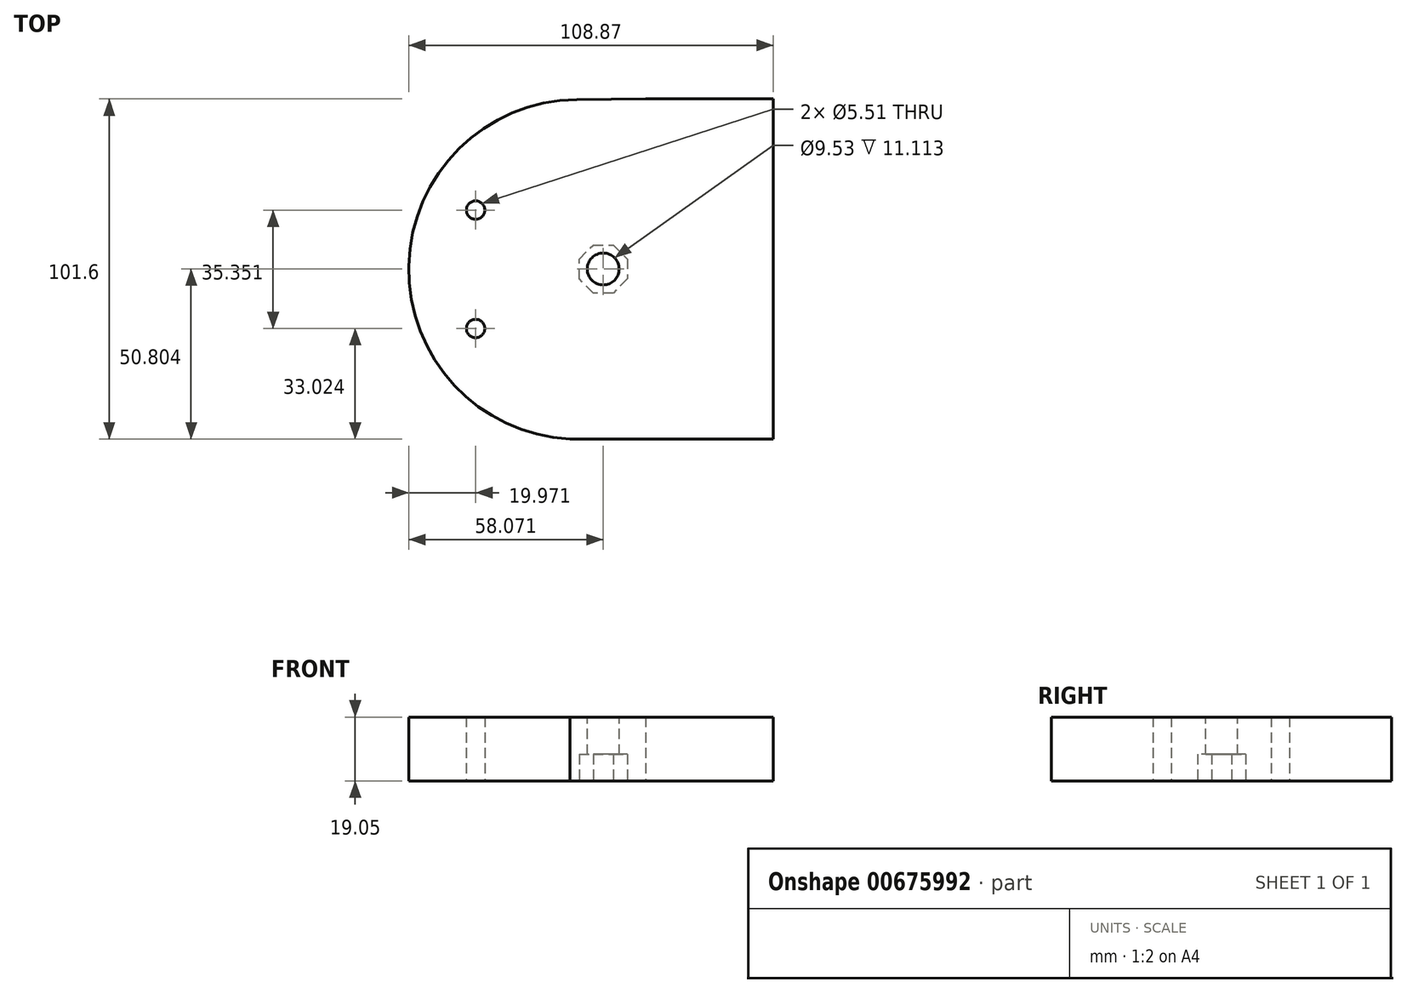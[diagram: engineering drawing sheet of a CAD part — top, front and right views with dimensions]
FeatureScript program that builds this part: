
annotation { "Feature Type Name" : "Feature", "Feature Type Description" : "" }
export const myFeature = defineFeature(function(context is Context, id is Id, definition is map)
    precondition{}
    {
        {
            var Q0;
            Q0=qCreatedBy(makeId("Top.planeOp"),FACE);
            var sketch = newSketch(context, id + "F0", { "sketchPlane" : qUnion([Q0])});
            skArc(sketch, "E0", {"start": v(-76.55, 44.5) * mm, "mid": v(-126.76, -5.22) * mm, "end": v(-78.58, -56.9) * mm});
            skLineSegment(sketch, "E1", {"start": v(-76.55, 44.5) * mm, "end": v(-56, 44.7) * mm});
            skLineSegment(sketch, "E2", {"start": v(-56, 44.7) * mm, "end": v(-56, -56.9) * mm});
            skLineSegment(sketch, "E3", {"start": v(-56, -56.9) * mm, "end": v(-78.58, -56.9) * mm});
            skCircle(sketch, "E4", {"center": v(-106.8, 11.47) * mm, "radius": 2.76 * mm});
            skCircle(sketch, "E5", {"center": v(-106.8, -23.88) * mm, "radius": 2.76 * mm});
            skSolve(sketch);
        }
        {
            var Q0;
            Q0 = qSketchRegion(id + "F0", true);
            extrude(context, id + "F1", {"entities" : qUnion([Q0]), "depth" : 19.05 * mm, "offsetDistance" : 25.4 * mm});
        }
        {
            var Q0;
            Q0=makeQuery(id+"F1.opExtrude","SWEPT_FACE",FACE,{"disambiguationData":[OSD([sQuery(id+"F0.wireOp",EDGE,"E2")])]});
            extrude(context, id + "F2", {"entities" : qUnion([Q0]), "operationType" : NewBodyOperationType.ADD, "depth" : 12.7 * mm, "offsetDistance" : 25.4 * mm});
        }
        {
            var Q0;
            Q0=makeQuery(id+"F2.opExtrude","CAP_FACE",FACE,{"disambiguationData":[OSD([sQuery(id+"F0.wireOp",EDGE,"E2")])],"isStart":false});
            extrude(context, id + "F3", {"entities" : qUnion([Q0]), "operationType" : NewBodyOperationType.ADD, "depth" : 25.4 * mm, "offsetDistance" : 25.4 * mm});
        }
        {
            var Q0;
            {var subQ0=sQuery(id+"F0.wireOp",EDGE,"E2");var subQ1=makeQuery(id+"F1.opExtrude","CAP_EDGE",EDGE,{"disambiguationData":[OSD([subQ0])],"isStart":false});Q0=makeQuery(id+"F3.boolean.opBoolean","MERGE",FACE,{"derivedFrom":[makeQuery(id+"F2.boolean.opBoolean","MERGE",FACE,{"derivedFrom":[makeQuery(id+"F1.opExtrude","CAP_FACE",FACE,{"disambiguationData":[OSD([sQuery(id+"F0.wireOp",EDGE,"E0"),sQuery(id+"F0.wireOp",EDGE,"E1"),subQ0,sQuery(id+"F0.wireOp",EDGE,"E3"),sQuery(id+"F0.wireOp",EDGE,"E4"),sQuery(id+"F0.wireOp",EDGE,"E5")])],"isStart":false}),makeQuery(id+"F2.opExtrude","SWEPT_FACE",FACE,{"disambiguationData":[OSD([subQ0]),TDD([subQ1])]})]}),makeQuery(id+"F3.opExtrude","SWEPT_FACE",FACE,{"disambiguationData":[OSD([subQ0]),TDD([makeQuery(id+"F2.opExtrude","CAP_EDGE",EDGE,{"disambiguationData":[OSD([subQ0]),TDD([subQ1])],"isStart":false})])]})]});}
            var sketch = newSketch(context, id + "F4", { "sketchPlane" : qUnion([Q0])});
            skCircle(sketch, "E6", {"center": v(-68.7, -6.1) * mm, "radius": 4.76 * mm});
            skSolve(sketch);
        }
        {
            var Q0;
            Q0=makeQuery(id+"F4.imprint","IMPRINT",FACE,{"disambiguationData":[TD([[makeQuery(id+"F4.imprint","IMPRINT",EDGE,{"derivedFrom":sQuery(id+"F4.wireOp",EDGE,"E6")}),1.0]])]});
            extrude(context, id + "F5", {"entities" : qUnion([Q0]), "operationType" : NewBodyOperationType.REMOVE, "endBound" : BoundingType.THROUGH_ALL, "oppositeDirection" : true, "depth" : 25.4 * mm, "offsetDistance" : 25.4 * mm});
        }
        {
            var Q0;
            {var subQ0=sQuery(id+"F0.wireOp",EDGE,"E2");var subQ1=makeQuery(id+"F1.opExtrude","CAP_EDGE",EDGE,{"disambiguationData":[OSD([subQ0])],"isStart":true});Q0=makeQuery(id+"F3.boolean.opBoolean","MERGE",FACE,{"derivedFrom":[makeQuery(id+"F2.boolean.opBoolean","MERGE",FACE,{"derivedFrom":[makeQuery(id+"F1.opExtrude","CAP_FACE",FACE,{"disambiguationData":[OSD([sQuery(id+"F0.wireOp",EDGE,"E0"),sQuery(id+"F0.wireOp",EDGE,"E1"),subQ0,sQuery(id+"F0.wireOp",EDGE,"E3"),sQuery(id+"F0.wireOp",EDGE,"E4"),sQuery(id+"F0.wireOp",EDGE,"E5")])],"isStart":true}),makeQuery(id+"F2.opExtrude","SWEPT_FACE",FACE,{"disambiguationData":[OSD([subQ0]),TDD([subQ1])]})]}),makeQuery(id+"F3.opExtrude","SWEPT_FACE",FACE,{"disambiguationData":[OSD([subQ0]),TDD([makeQuery(id+"F2.opExtrude","CAP_EDGE",EDGE,{"disambiguationData":[OSD([subQ0]),TDD([subQ1])],"isStart":false})])]})]});}
            var sketch = newSketch(context, id + "F6", { "sketchPlane" : qUnion([Q0])});
            skLineSegment(sketch, "E7", {"start": v(-71.67, -1.07) * mm, "end": v(-65.71, -1.07) * mm});
            skLineSegment(sketch, "E8", {"start": v(-65.71, -1.07) * mm, "end": v(-61.54, 3.1) * mm});
            skLineSegment(sketch, "E9", {"start": v(-61.54, 3.1) * mm, "end": v(-61.54, 9.06) * mm});
            skLineSegment(sketch, "E10", {"start": v(-61.54, 9.06) * mm, "end": v(-65.73, 13.26) * mm});
            skLineSegment(sketch, "E11", {"start": v(-65.73, 13.26) * mm, "end": v(-71.67, 13.26) * mm});
            skLineSegment(sketch, "E12", {"start": v(-71.67, 13.26) * mm, "end": v(-75.86, 9.06) * mm});
            skLineSegment(sketch, "E13", {"start": v(-75.86, 9.06) * mm, "end": v(-75.86, 3.13) * mm});
            skLineSegment(sketch, "E14", {"start": v(-75.86, 3.13) * mm, "end": v(-71.67, -1.07) * mm});
            skSolve(sketch);
        }
        {
            var Q0;
            Q0=makeQuery(id+"F6.imprint","IMPRINT",FACE,{"disambiguationData":[TD([[makeQuery(id+"F6.imprint","IMPRINT",EDGE,{"derivedFrom":sQuery(id+"F6.wireOp",EDGE,"E7")}),1.0]])]});
            extrude(context, id + "F7", {"entities" : qUnion([Q0]), "operationType" : NewBodyOperationType.REMOVE, "oppositeDirection" : true, "depth" : 7.94 * mm, "offsetDistance" : 25.4 * mm});
        }
    });
